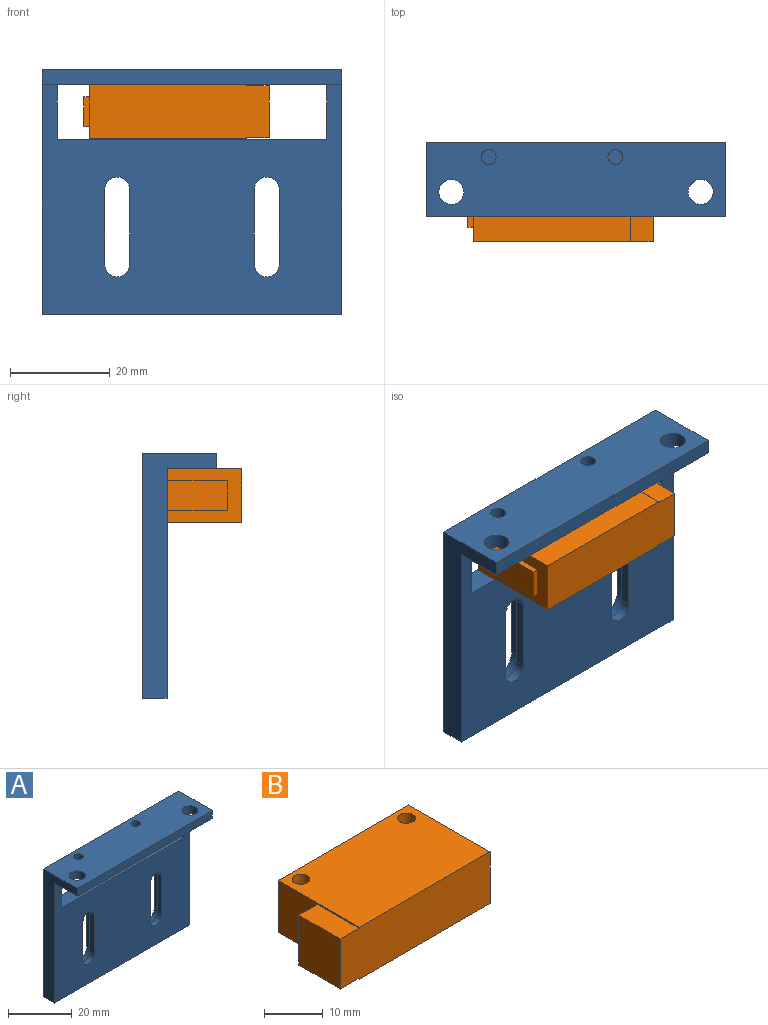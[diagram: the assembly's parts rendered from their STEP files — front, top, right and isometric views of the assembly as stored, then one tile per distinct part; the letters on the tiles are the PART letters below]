
ASSEMBLY  parts=2 mates=1
PART A: 33 faces, bbox 60x15x49 mm
  f0: plane 54x5mm, normal (0,0,1), area 270mm2, adj f6,f23,f24,f26
  f1: cylinder r=2.5mm len=5mm, axis (0,-1,0), area 15.7mm2, adj f2,f4,f5,f6
  f2: plane 15x2mm, normal (-1,0,0), area 30mm2, adj f1,f3,f5,f6
  f3: cylinder r=2.5mm len=5mm, axis (0,-1,0), area 15.7mm2, adj f2,f4,f5,f6
  f4: plane 15x2mm, normal (1,0,0), area 30mm2, adj f1,f3,f5,f6
  f5: plane 23.5x8.5mm, normal (0,1,0), area 89.6mm2, adj f1,f2,f3,f4,f7,f8,f9,f10
  f6: plane 60x46mm, normal (0,-1,0), area 1976.7mm2, adj f0,f1,f2,f3,f4,f11,f12,f13
  f7: plane 15x3mm, normal (1,0,0), area 45mm2, adj f5,f9,f10,f23
  f8: plane 15x3mm, normal (-1,0,0), area 45mm2, adj f5,f9,f10,f23
  f9: cylinder r=4.25mm len=8.5mm, axis (0,-1,0), area 40.1mm2, adj f5,f7,f8,f23
  f10: cylinder r=4.25mm len=8.5mm, axis (0,-1,0), area 40.1mm2, adj f5,f7,f8,f23
  f11: cylinder r=2.5mm len=5mm, axis (0,-1,0), area 15.7mm2, adj f6,f12,f14,f15
  f12: plane 15x2mm, normal (-1,0,0), area 30mm2, adj f6,f11,f13,f15
  f13: cylinder r=2.5mm len=5mm, axis (0,-1,0), area 15.7mm2, adj f6,f12,f14,f15
  f14: plane 15x2mm, normal (1,0,0), area 30mm2, adj f6,f11,f13,f15
  f15: plane 23.5x8.5mm, normal (0,1,0), area 89.6mm2, adj f11,f12,f13,f14,f16,f17,f18,f19
  f16: plane 15x3mm, normal (1,0,0), area 45mm2, adj f15,f18,f19,f23
  f17: plane 15x3mm, normal (-1,0,0), area 45mm2, adj f15,f18,f19,f23
  f18: cylinder r=4.25mm len=8.5mm, axis (0,-1,0), area 40.1mm2, adj f15,f16,f17,f23
  f19: cylinder r=4.25mm len=8.5mm, axis (0,-1,0), area 40.1mm2, adj f15,f16,f17,f23
  f20: plane 49x15mm, normal (-1,0,0), area 275mm2, adj f6,f21,f23,f25,f27,f28
  f21: plane 60x5mm, normal (0,0,-1), area 300mm2, adj f6,f20,f22,f23
  f22: plane 49x15mm, normal (1,0,0), area 275mm2, adj f6,f21,f23,f25,f27,f28
  f23: plane 60x49mm, normal (0,1,0), area 1977.5mm2, adj f0,f7,f8,f9,f10,f16,f17,f18
  f24: plane 11x5mm, normal (1,0,0), area 55mm2, adj f0,f6,f23,f25
  f25: plane 60x15mm, normal (0,0,-1), area 816.6mm2, adj f6,f20,f22,f23,f24,f26,f28,f29
  f26: plane 11x5mm, normal (-1,0,0), area 55mm2, adj f0,f6,f23,f25
  f27: plane 60x15mm, normal (0,0,1), area 846.6mm2, adj f20,f22,f23,f28,f29,f30,f31,f32
  f28: plane 60x3mm, normal (0,-1,0), area 180mm2, adj f20,f22,f25,f27
  f29: cylinder r=2.5mm len=5mm, axis (0,0,1), area 47.1mm2, adj f25,f27
  f30: cylinder r=2.5mm len=5mm, axis (0,0,1), area 47.1mm2, adj f25,f27
  f31: cylinder r=1.5mm len=3mm, axis (0,0,1), area 28.3mm2, adj f25,f27
  f32: cylinder r=1.5mm len=3mm, axis (0,0,1), area 28.3mm2, adj f25,f27
PART B: 17 faces, bbox 37.2x19.5x10.8 mm
  f0: plane 19.5x10.8mm, normal (1,0,0), area 120.6mm2, adj f2,f5,f6,f7,f12,f13,f15,f16
  f1: plane 19.5x10.8mm, normal (-1,0,0), area 106.6mm2, adj f2,f5,f6,f7,f8,f10,f11
  f2: plane 36x10.8mm, normal (0,-1,0), area 387mm2, adj f0,f1,f6,f7,f9,f10,f11
  f3: cylinder r=1.5mm len=10.8mm, axis (0,0,-1), area 101.8mm2, adj f6,f7
  f4: cylinder r=1.5mm len=10.8mm, axis (0,0,-1), area 101.8mm2, adj f6,f7
  f5: plane 31.5x10.8mm, normal (0,1,0), area 340.2mm2, adj f0,f1,f6,f7
  f6: plane 31.5x19.5mm, normal (0,0,1), area 600.1mm2, adj f0,f1,f2,f3,f4,f5
  f7: plane 31.5x19.5mm, normal (0,0,-1), area 600.1mm2, adj f0,f1,f2,f3,f4,f5
  f8: plane 10.4x4.5mm, normal (0,1,0), area 46.8mm2, adj f1,f9,f10,f11
  f9: plane 10.4x10mm, normal (-1,0,0), area 104mm2, adj f2,f8,f10,f11
  f10: plane 10x4.5mm, normal (0,0,1), area 45mm2, adj f1,f2,f8,f9
  f11: plane 10x4.5mm, normal (0,0,-1), area 45mm2, adj f1,f2,f8,f9
  f12: plane 6x1.15mm, normal (0,1,0), area 6.9mm2, adj f0,f14,f15,f16
  f13: plane 6x1.15mm, normal (0,-1,0), area 6.9mm2, adj f0,f14,f15,f16
  f14: plane 15x6mm, normal (1,0,0), area 90mm2, adj f12,f13,f15,f16
  f15: plane 15x1.15mm, normal (0,0,1), area 17.2mm2, adj f0,f12,f13,f14
  f16: plane 15x1.15mm, normal (0,0,-1), area 17.2mm2, adj f0,f12,f13,f14
PLACE A t=(-24.54,61.21,-23.61)mm
PLACE B rot(axis=(0,1,0),180deg) t=(-29.34,55.96,-0.51)mm
MATE fastened A.f32 <-> B.f4  axis (0,0,-1) through (-42.04,63.21,4.89)mm
